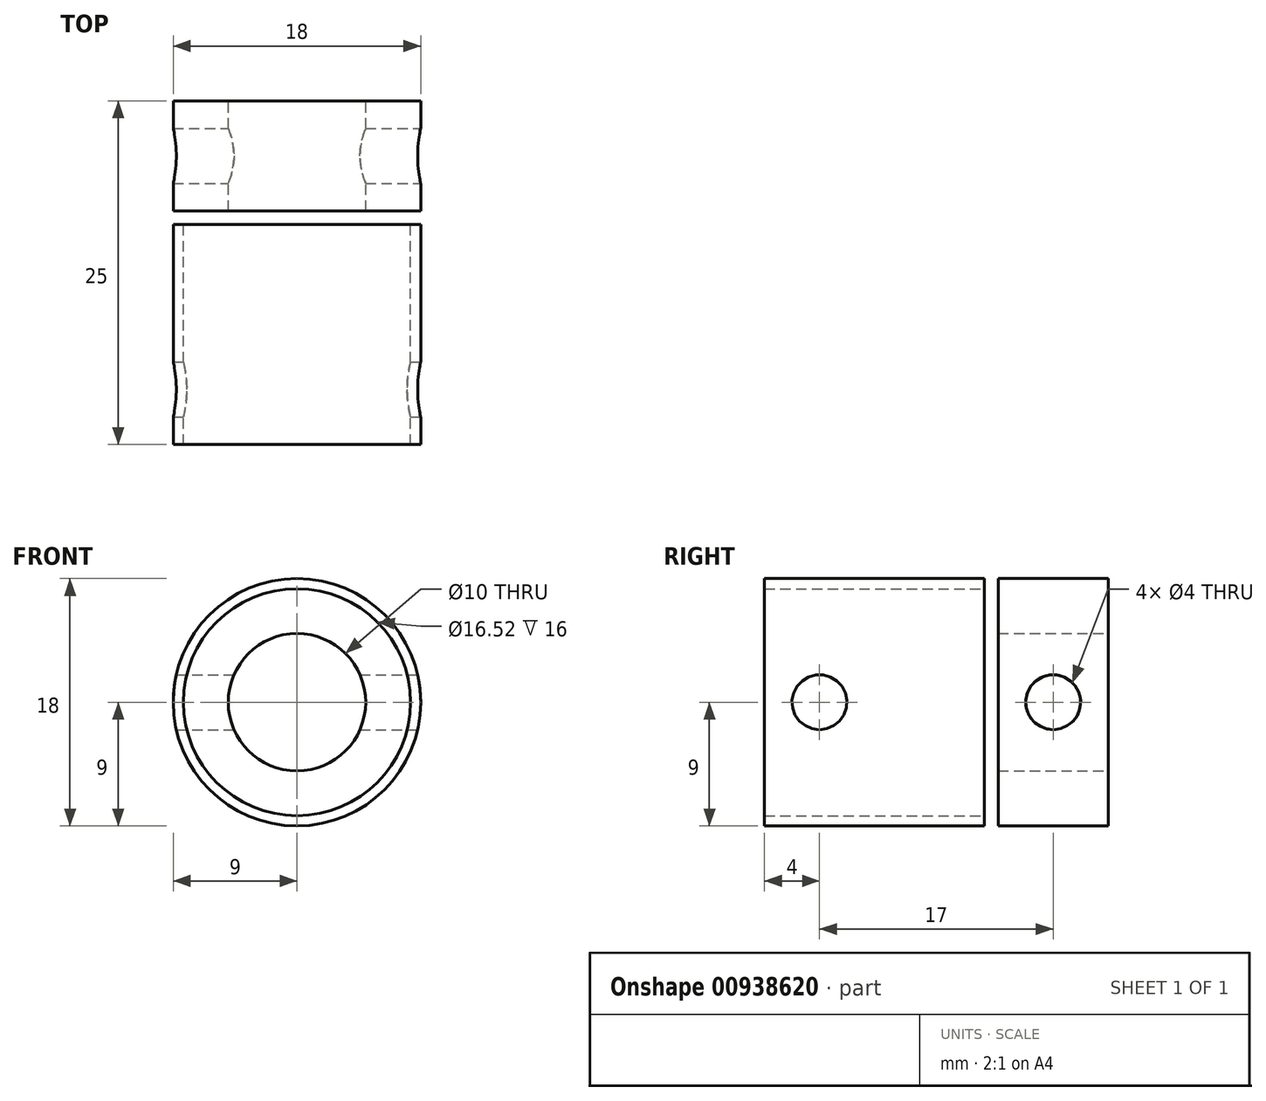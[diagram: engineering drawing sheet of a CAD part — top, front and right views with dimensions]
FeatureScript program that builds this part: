
annotation { "Feature Type Name" : "Feature", "Feature Type Description" : "" }
export const myFeature = defineFeature(function(context is Context, id is Id, definition is map)
    precondition{}
    {
        {
            var Q0;
            Q0=qCreatedBy(makeId("Front.planeOp"),FACE);
            var sketch = newSketch(context, id + "F0", { "sketchPlane" : qUnion([Q0])});
            skCircle(sketch, "E0", {"center": v(0, 0) * mm, "radius": 9 * mm});
            skSolve(sketch);
        }
        {
            var Q0;
            Q0=makeQuery(id+"F0.imprint","IMPRINT",FACE,{"disambiguationData":[TD([[makeQuery(id+"F0.imprint","IMPRINT",EDGE,{"derivedFrom":sQuery(id+"F0.wireOp",EDGE,"E0")}),1.0]])]});
            extrude(context, id + "F1", {"entities" : qUnion([Q0]), "depth" : 25 * mm, "offsetDistance" : 25 * mm});
        }
        {
            var Q0;
            Q0=makeQuery(id+"F1.opExtrude","CAP_FACE",FACE,{"disambiguationData":[OSD([sQuery(id+"F0.wireOp",EDGE,"E0")])],"isStart":true});
            var sketch = newSketch(context, id + "F2", { "sketchPlane" : qUnion([Q0])});
            skCircle(sketch, "E1", {"center": v(0, 0) * mm, "radius": 5 * mm});
            skSolve(sketch);
        }
        {
            var Q0;
            Q0=makeQuery(id+"F2.imprint","IMPRINT",FACE,{"disambiguationData":[TD([[makeQuery(id+"F2.imprint","IMPRINT",EDGE,{"derivedFrom":sQuery(id+"F2.wireOp",EDGE,"E1")}),1.0]])]});
            extrude(context, id + "F3", {"entities" : qUnion([Q0]), "operationType" : NewBodyOperationType.REMOVE, "oppositeDirection" : true, "depth" : 10 * mm, "offsetDistance" : 25 * mm});
        }
        {
            var Q0;
            Q0=makeQuery(id+"F1.opExtrude","CAP_FACE",FACE,{"disambiguationData":[OSD([sQuery(id+"F0.wireOp",EDGE,"E0")])],"isStart":false});
            var sketch = newSketch(context, id + "F4", { "sketchPlane" : qUnion([Q0])});
            skCircle(sketch, "E2", {"center": v(0, 0) * mm, "radius": 4 * mm});
            skSolve(sketch);
        }
        {
            var Q0;
            Q0=makeQuery(id+"F4.imprint","IMPRINT",FACE,{"disambiguationData":[TD([[makeQuery(id+"F4.imprint","IMPRINT",EDGE,{"derivedFrom":sQuery(id+"F4.wireOp",EDGE,"E2")}),1.0]])]});
            extrude(context, id + "F5", {"entities" : qUnion([Q0]), "operationType" : NewBodyOperationType.REMOVE, "oppositeDirection" : true, "depth" : 8 * mm, "offsetDistance" : 25 * mm});
        }
        {
            var Q0;
            Q0=qCreatedBy(makeId("Right.planeOp"),FACE);
            var sketch = newSketch(context, id + "F6", { "sketchPlane" : qUnion([Q0])});
            skCircle(sketch, "E3", {"center": v(-4, 0) * mm, "radius": 2 * mm});
            skCircle(sketch, "E4", {"center": v(-21, 0) * mm, "radius": 2 * mm});
            skSolve(sketch);
        }
        {
            var Q0;
            Q0=makeQuery(id+"F6.imprint","IMPRINT",FACE,{"disambiguationData":[TD([[makeQuery(id+"F6.imprint","IMPRINT",EDGE,{"derivedFrom":sQuery(id+"F6.wireOp",EDGE,"E4")}),1.0]])]});
            var Q1;
            Q1=makeQuery(id+"F6.imprint","IMPRINT",FACE,{"disambiguationData":[TD([[makeQuery(id+"F6.imprint","IMPRINT",EDGE,{"derivedFrom":sQuery(id+"F6.wireOp",EDGE,"E3")}),1.0]])]});
            extrude(context, id + "F7", {"entities" : qUnion([Q0, Q1]), "operationType" : NewBodyOperationType.REMOVE, "endBound" : BoundingType.THROUGH_ALL, "oppositeDirection" : true, "depth" : 25 * mm, "offsetDistance" : 25 * mm, "hasSecondDirection" : true, "secondDirectionBound" : SecondDirectionBoundingType.THROUGH_ALL, "secondDirectionOppositeDirection" : false, "secondDirectionDepth" : 25 * mm});
        }
        {
            var Q0;
            Q0=qCreatedBy(makeId("Front.planeOp"),FACE);
            cPlane(context, id + "F8", {"entities" : qUnion([Q0]), "cplaneType" : CPlaneType.OFFSET, "offset" : 8 * mm, "width" : 150 * mm, "height" : 150 * mm});
        }
        {
            var Q0;
            Q0=qCreatedBy(id+"F8.planeOp",FACE);
            var sketch = newSketch(context, id + "F9", { "sketchPlane" : qUnion([Q0])});
            skCircle(sketch, "E5", {"center": v(0, 0) * mm, "radius": 9.7 * mm});
            skSolve(sketch);
        }
        {
            var Q0;
            Q0=makeQuery(id+"F9.imprint","IMPRINT",FACE,{"disambiguationData":[TD([[makeQuery(id+"F9.imprint","IMPRINT",EDGE,{"derivedFrom":sQuery(id+"F9.wireOp",EDGE,"E5")}),1.0]])]});
            extrude(context, id + "F10", {"entities" : qUnion([Q0]), "depth" : 1 * mm, "offsetDistance" : 25 * mm});
        }
        {
            var Q0;
            Q0=makeQuery(id+"F10.opExtrude","CAP_FACE",FACE,{"disambiguationData":[OSD([sQuery(id+"F9.wireOp",EDGE,"E5")])],"isStart":true});
            var sketch = newSketch(context, id + "F11", { "sketchPlane" : qUnion([Q0])});
            skCircle(sketch, "E6", {"center": v(0, 0) * mm, "radius": 8.26 * mm});
            skSolve(sketch);
        }
        {
            var Q0;
            Q0=makeQuery(id+"F11.imprint","IMPRINT",FACE,{"disambiguationData":[TD([[makeQuery(id+"F11.imprint","IMPRINT",EDGE,{"derivedFrom":sQuery(id+"F11.wireOp",EDGE,"E6")}),1.0]])]});
            extrude(context, id + "F12", {"entities" : qUnion([Q0]), "operationType" : NewBodyOperationType.REMOVE, "endBound" : BoundingType.THROUGH_ALL, "oppositeDirection" : true, "depth" : 25 * mm, "offsetDistance" : 25 * mm});
        }
        {
            var Q0;
            Q0=makeQuery(id+"F10.opExtrude","SWEPT_BODY",BODY,{"disambiguationData":[OSD([sQuery(id+"F9.wireOp",EDGE,"E5")])]});
            var Q1;
            Q1=makeQuery(id+"F1.opExtrude","SWEPT_BODY",BODY,{"disambiguationData":[OSD([sQuery(id+"F0.wireOp",EDGE,"E0")])]});
            booleanBodies(context, id + "F13", {"operationType" : BooleanOperationType.SUBTRACTION, "tools" : qUnion([Q0]), "targets" : qUnion([Q1])});
        }
    });
